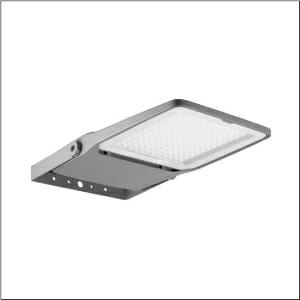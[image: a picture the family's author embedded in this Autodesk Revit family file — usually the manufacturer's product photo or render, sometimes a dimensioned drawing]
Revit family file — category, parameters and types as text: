
# Revit family: floodlight_fl_20_midi___pl43_5xa7682d3a2ac_b539
name_source: partatom
category: Lighting Fixtures
units: mm (PartAtom-declared; Revit-internal decimal feet)

## family parameters
Cut with Voids When Loaded = No
Host = Face
Light Source = No
Part Type = Normal
Room Calculation Point = No
Round Connector Dimension = Use Diameter
Shared = No

## types (1)
- --- (1 x LED 5000K / CRI = 70 (unbekannt), 19360 lm, 5000K)
    Apparent Load = 142 VA
    CIE Flux Codes = 32 74 99 100 100
    Color Rendering = 70
    Color Temperature = 5000K
    Default Elevation = 1800 mm
    Description = Floodlight FL 20 midi, floodlight, primary light control with lens, of plastic, primary optical cover: protective disc, of toughened safety glass, transparent, light distribution: PL43, light emission: direct distribution, primary light characteristic: asymmetric, installation type: surface-mounted, LED, High Power LED, rated luminous flux: 19.360lm, luminous efficacy: 136lm/W, light colour: 750, colour temperature: 5000K, control gear: ECG Plus, control: flexible luminous flux parameterisation, time-dependent luminous flux control, digital communication interface, power reduction, overheat protection, electronic power reduction, with terminal, 5-pole, max. 2.5mm², mains connection: 220..240V, AC, 50/60Hz, rated input power: 142W, LED unit, of diecast aluminium, powder-coated, Siteco® metallic grey (DB 702S), corrosivity category C5 mid according to DIN EN ISO 12944, incl. 1x M20 cable gland for cable Ø 6.5..12mm, length: 731mm, width: 450mm, height: 76mm, housing frame, of diecast aluminium, powder-coated, Siteco® metallic grey (DB 702S), wall fastening, of steel, powder-coated, Siteco® metallic grey (DB 702S), DALI, protection rating (complete): IP66, insulation class (complete): insulation class II (safety insulation), certification: CE, ENEC, VDE, protection symbol: D, permissible operating ambient temperature: -40..+40°C, permissible operating ambient temperature for outdoor applications: -40..+50°C, standard: DIN EN 12944, packaging unit: 1 piece

Light Distribution: PL43
    Height = 76 mm
    Lamp = 1 x LED 5000K / CRI >= 70 (unbekannt)
    Lamp Light Flux = 19360 lm
    Lamp count = 1
    Length = 731 mm
    Luminous efficacy = 136 lm/W
    Manufacturer = Siteco
    ModVariant = No
    Model = 5XA7682D3A2AC
    Mounting Place = Wall
    Mounting Type = Surface mounted
    Number of Poles = 1
    OnlyDefault = Yes
    Power Factor = 1
    Product Name = Floodlight FL 20 midi | PL43
    Product group = floodlight | wall mounted
    ProductGroupID = 2001
    Protection Class = Protection class II
    Protection Degree = IP 66
    RLX_Detail_Level = 1
    RLX_Emergency_Light_Flux = 0 lm
    RLX_Emergency_Type = 0
    RLX_Emergency_Type_DB = No
    RlxData = <blob elided: 92013 chars, md5=433a4fc9>
    Socket = socket
    Standby Power = 0 W
    System Light Flux = 19360 lm
    System Power = 142 W
    Type Comments = factory setting: luminous flux: 100 % | dim-lin: 254 | 489 mA
    Type Image = l_1005944.jpg
    URL = http://relux.com
    VarID = @adj_148511
    Voltage = 0 V
    Weight = 0.00 kg
    Width = 450 mm

## geometry (parser evidence)
native form markers: Blend x4, Sweep x15
no freeform markers — native parametric forms only
